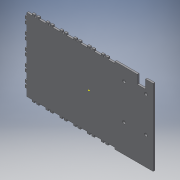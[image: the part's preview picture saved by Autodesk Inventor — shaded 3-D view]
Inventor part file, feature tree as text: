
AUTODESK INVENTOR PART (.ipt)
format: ipt  version: 2016 (Build 200138000, 138)  size: 374,784 bytes
history: native  units: in
note: dims shown in document units (in); Inventor stores cm internally (conversion verified against a paired STEP export)
features: sketch x18, extrude x16, pattern_linear x2, mirror x1, projected_geometry x1
ambient origin geometry x8: Origin, YZ Plane, XZ Plane, XY Plane, X Axis, Y Axis, Z Axis, Center Point
bodies: Solid1 (feature_tree)
feature tree (38):
  extrude  "Extrusion1"  Depth=5.5118in
  extrude  "Extrusion2"  Depth=0.125in
  extrude  "Extrusion3"  Depth=0.2165in
  extrude  "Extrusion4"  Depth=0.9252in
  pattern_linear  "Rectangular Pattern1"  Count1=4  [1 undecoded]
  extrude  "Extrusion5"  Depth=0.5315in
  extrude  "Extrusion6"  Depth=0.2165in
  extrude  "Extrusion7"  Depth=2.5591in
  extrude  "Extrusion8"  Depth=0.5in
  extrude  "Extrusion9"  Depth=0.125in TaperAngle=0.0deg
  extrude  "Extrusion10"  Depth=0.125in
  extrude  "Extrusion11"  Depth=0.18in TaperAngle=0.0deg
  extrude  "Extrusion12"  Depth=1.0in
  pattern_linear  "Rectangular Pattern2"  Count1=10  [1 undecoded]
  extrude  "Extrusion13"  Depth=0.5906in
  sketch  "Sketch14"  dims[d34=0.3937in d35=0.0in d36=0.126in]
  sketch  "Sketch15"  dims[d37=0.1988in d38=0.0394in]
  extrude  "Extrusion14"  Depth=0.3937in
  extrude  "Extrusion15"  Depth=0.0394in
  extrude  "Extrusion16"  Depth=0.0394in
  mirror  "Mirror1"
  sketch  "Sketch1"  dims[d0=9.2638in d1=5.5118in]
  sketch  "Sketch2"  dims[d2=0.125in d3=0.0in d4=0.9252in]
  sketch  "Sketch3"  dims[d5=0.5315in d6=0.2165in]
  sketch  "Sketch4"  dims[d7=0.2165in d8=0.9252in d9=1.5748in]
  sketch  "Sketch5"  dims[d10=0.2165in d11=0.5315in]
  sketch  "Sketch6"  dims[d12=2.5591in d13=0.2165in]
  sketch  "Sketch7"  dims[d14=1.5748in d15=2.5591in]
  sketch  "Sketch8"  dims[d16=0.25in d17=0.0in d18=0.5in]
  sketch  "Sketch9"  dims[d19=0.125in d20=0.25in d21=0.0in]
  projected_geometry  "Projected Loop1"
  sketch  "Sketch10"  dims[d22=0.14in d23=0.125in]
  sketch  "Sketch11"  dims[d24=0.18in d25=0.25in d26=0.0in]
  sketch  "Sketch12"  dims[d27=2.3622in d29=1.0in d30=6.4567in d31=3.937in]
  sketch  "Sketch13"  dims[d32=0.5906in d33=1.378in]
  sketch  "Sketch16"  dims[d39=0.126in d40=0.0394in]
  sketch  "Sketch17"  dims[d41=0.1988in]
  sketch  "Sketch18"  dims[d42=0.126in d43=0.0394in d44=0.1988in d45=0.126in d46=0.0394in d47=0.1988in d48=0.3937in d49=0.0in d50=0.25in d51=0.5in d52=0.5in d53=0.3937in d54=0.0in d55=0.14in d56=0.18in d57=0.1in d58=0.3937in d59=0.0in d60=0.1094in d61=0.3125in d63=0.3937in d64=0.0in d65=0.0863in d66=0.0863in d67=0.0in d68=0.6in d69=0.3937in d70=0.0in d71=0.125in d72=0.5in d73=0.3937in d74=0.0in d75=0.138in d76=0.125in d77=0.181in d78=0.3937in d79=0.0in d80=1.9685in d82=1.0in d83=0.25in d84=0.181in d85=0.3937in d86=0.0in d87=0.5906in d88=0.5512in d89=0.3937in d90=0.0in d91=0.125in d92=0.181in d93=0.3937in d94=0.0in d95=0.125in d96=0.5in d97=0.18in d98=0.3937in d99=0.0in]
note: 2 required parameter values undecoded (feature->parameter linkage not recoverable at this tier; creation-order binding heuristic only, values carry confidence <= 0.55)
